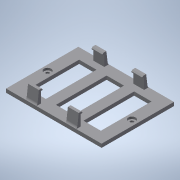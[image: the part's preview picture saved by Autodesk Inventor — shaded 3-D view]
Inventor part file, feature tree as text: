
AUTODESK INVENTOR PART (.ipt)
format: ipt  version: 2020 (Build 240168000, 168)  size: 444,416 bytes
history: native  units: in
note: dims shown in document units (in); Inventor stores cm internally (conversion verified against a paired STEP export)
features: extrude x8, sketch x8, fillet x1
ambient origin geometry x8: Origin, YZ Plane, XZ Plane, XY Plane, X Axis, Y Axis, Z Axis, Center Point
bodies: Solid1 (feature_tree)
feature tree (17):
  extrude  "Extrusion1"  Depth=2.5in
  extrude  "Extrusion4"  Depth=0.438in TaperAngle=0.0deg
  extrude  "Extrusion5"  Depth=0.125in
  fillet  "Fillet1"  Radius=1.75in
  extrude  "Extrusion6"  Depth=0.063in TaperAngle=0.0deg
  extrude  "Extrusion7"  Depth=1.75in
  extrude  "Extrusion8"  Depth=0.125in TaperAngle=0.0deg
  extrude  "Extrusion9"  Depth=0.35in
  extrude  "Extrusion12"  Depth=0.6in
  sketch  "Sketch1"  dims[d0=3.3in d1=2.5in]
  sketch  "Sketch4"  dims[d2=0.125in d3=0.0in d15=0.438in d16=0.0in]
  sketch  "Sketch5"  dims[d17=0.07in d18=0.125in d19=1.75in d20=0.0in]
  sketch  "Sketch6"  dims[d21=0.125in d23=0.063in d24=0.0in]
  sketch  "Sketch7"  dims[d26=1.75in d27=0.0in d29=2.914in]
  sketch  "Sketch8"  dims[d30=0.075in d31=0.0in d32=0.125in d33=0.0in]
  sketch  "Sketch9"  dims[d41=0.4in d42=0.35in]
  sketch  "Sketch12"  dims[d43=0.35in d44=0.6in d45=0.6in d46=0.6in d47=0.2in d48=1.25in d49=1.25in d50=0.064in d51=0.064in d52=0.064in d53=0.064in d54=0.0in d55=0.01in d56=0.0in d57=0.5in d58=0.0344in]
